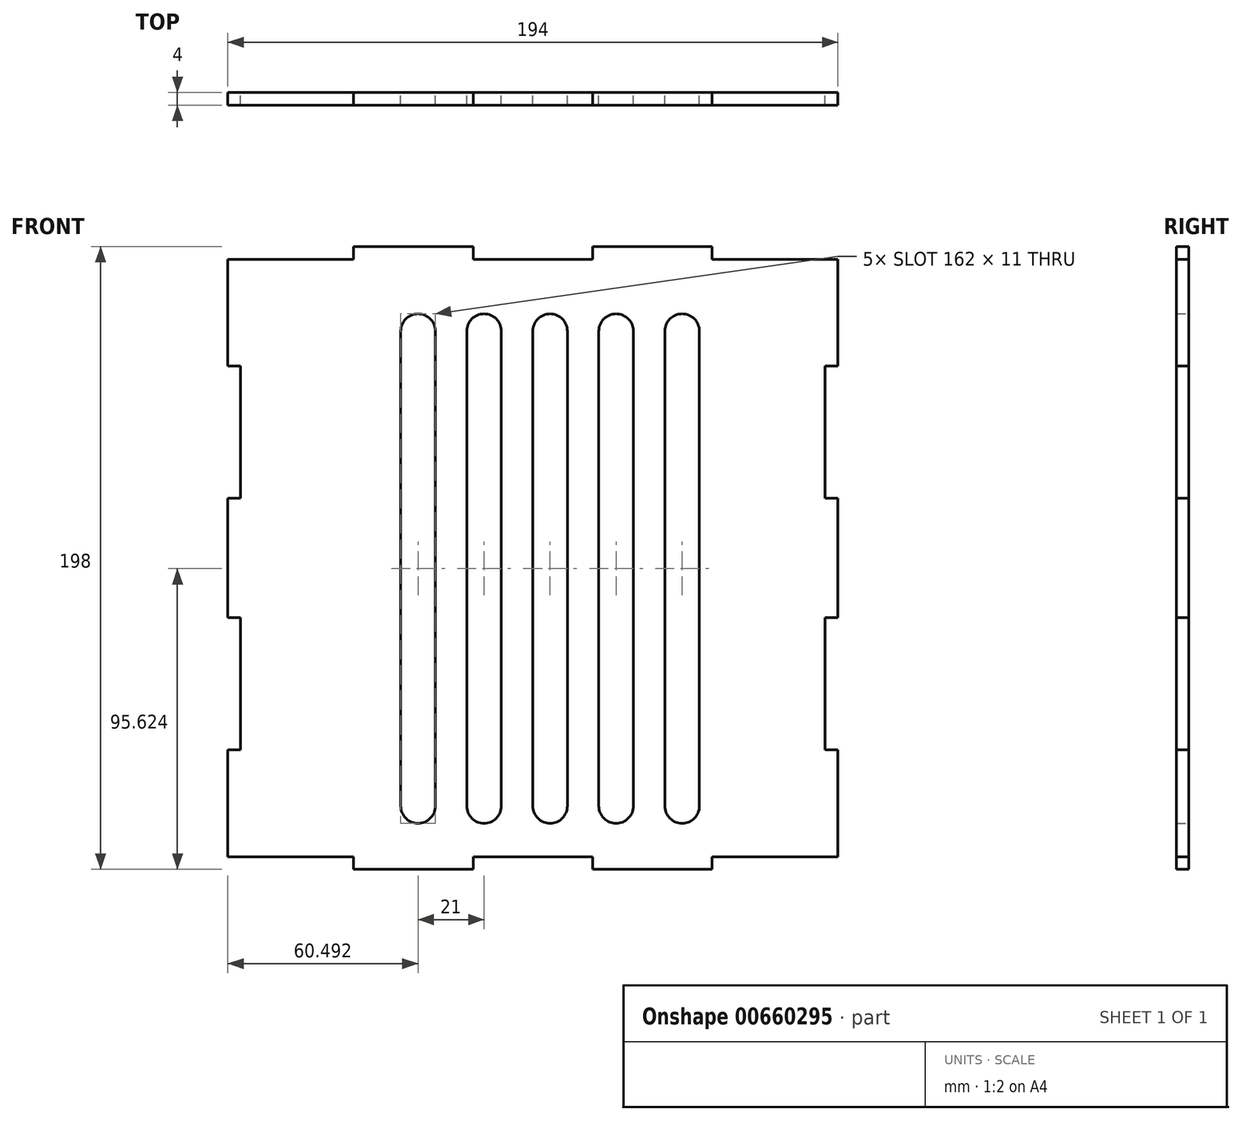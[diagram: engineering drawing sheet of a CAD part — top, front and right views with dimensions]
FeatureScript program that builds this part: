
annotation { "Feature Type Name" : "Feature", "Feature Type Description" : "" }
export const myFeature = defineFeature(function(context is Context, id is Id, definition is map)
    precondition{}
    {
        {
            var Q0;
            Q0=qCreatedBy(makeId("Front.planeOp"),FACE);
            var sketch = newSketch(context, id + "F0", { "sketchPlane" : qUnion([Q0])});
            skLineSegment(sketch, "E0.bottom", {"start": v(0, 0) * mm, "end": v(194, 0) * mm});
            skLineSegment(sketch, "E0.top", {"start": v(0, 198) * mm, "end": v(194, 198) * mm});
            skLineSegment(sketch, "E0.left", {"start": v(0, 0) * mm, "end": v(0, 198) * mm});
            skLineSegment(sketch, "E0.right", {"start": v(194, 0) * mm, "end": v(194, 198) * mm});
            skLineSegment(sketch, "E1.bottom", {"start": v(0, 0) * mm, "end": v(40, 0) * mm});
            skLineSegment(sketch, "E1.top", {"start": v(0, 4) * mm, "end": v(40, 4) * mm});
            skLineSegment(sketch, "E1.left", {"start": v(0, 0) * mm, "end": v(0, 4) * mm});
            skLineSegment(sketch, "E1.right", {"start": v(40, 0) * mm, "end": v(40, 4) * mm});
            skLineSegment(sketch, "E2.bottom", {"start": v(194, 0) * mm, "end": v(154, 0) * mm});
            skLineSegment(sketch, "E2.top", {"start": v(194, 4) * mm, "end": v(154, 4) * mm});
            skLineSegment(sketch, "E2.left", {"start": v(194, 0) * mm, "end": v(194, 4) * mm});
            skLineSegment(sketch, "E2.right", {"start": v(154, 0) * mm, "end": v(154, 4) * mm});
            skLineSegment(sketch, "E3.bottom", {"start": v(78, 0) * mm, "end": v(116, 0) * mm});
            skLineSegment(sketch, "E3.top", {"start": v(78, 4) * mm, "end": v(116, 4) * mm});
            skLineSegment(sketch, "E3.left", {"start": v(78, 0) * mm, "end": v(78, 4) * mm});
            skLineSegment(sketch, "E3.right", {"start": v(116, 0) * mm, "end": v(116, 4) * mm});
            skLineSegment(sketch, "E4.bottom", {"start": v(0, 198) * mm, "end": v(40, 198) * mm});
            skLineSegment(sketch, "E4.top", {"start": v(0, 194) * mm, "end": v(40, 194) * mm});
            skLineSegment(sketch, "E4.left", {"start": v(0, 198) * mm, "end": v(0, 194) * mm});
            skLineSegment(sketch, "E4.right", {"start": v(40, 198) * mm, "end": v(40, 194) * mm});
            skLineSegment(sketch, "E5.bottom", {"start": v(78, 198) * mm, "end": v(116, 198) * mm});
            skLineSegment(sketch, "E5.top", {"start": v(78, 194) * mm, "end": v(116, 194) * mm});
            skLineSegment(sketch, "E5.left", {"start": v(78, 198) * mm, "end": v(78, 194) * mm});
            skLineSegment(sketch, "E5.right", {"start": v(116, 198) * mm, "end": v(116, 194) * mm});
            skLineSegment(sketch, "E6.bottom", {"start": v(194, 198) * mm, "end": v(154, 198) * mm});
            skLineSegment(sketch, "E6.top", {"start": v(194, 194) * mm, "end": v(154, 194) * mm});
            skLineSegment(sketch, "E6.left", {"start": v(194, 198) * mm, "end": v(194, 194) * mm});
            skLineSegment(sketch, "E6.right", {"start": v(154, 198) * mm, "end": v(154, 194) * mm});
            skLineSegment(sketch, "E7.bottom", {"start": v(0, 38) * mm, "end": v(4, 38) * mm});
            skLineSegment(sketch, "E7.top", {"start": v(0, 80) * mm, "end": v(4, 80) * mm});
            skLineSegment(sketch, "E7.left", {"start": v(0, 38) * mm, "end": v(0, 80) * mm});
            skLineSegment(sketch, "E7.right", {"start": v(4, 38) * mm, "end": v(4, 80) * mm});
            skLineSegment(sketch, "E8.bottom", {"start": v(0, 160) * mm, "end": v(4, 160) * mm});
            skLineSegment(sketch, "E8.top", {"start": v(0, 118) * mm, "end": v(4, 118) * mm});
            skLineSegment(sketch, "E8.left", {"start": v(0, 160) * mm, "end": v(0, 118) * mm});
            skLineSegment(sketch, "E8.right", {"start": v(4, 160) * mm, "end": v(4, 118) * mm});
            skLineSegment(sketch, "E9.bottom", {"start": v(194, 80) * mm, "end": v(190, 80) * mm});
            skLineSegment(sketch, "E9.top", {"start": v(194, 38) * mm, "end": v(190, 38) * mm});
            skLineSegment(sketch, "E9.left", {"start": v(194, 80) * mm, "end": v(194, 38) * mm});
            skLineSegment(sketch, "E9.right", {"start": v(190, 80) * mm, "end": v(190, 38) * mm});
            skLineSegment(sketch, "E10.bottom", {"start": v(194, 160) * mm, "end": v(190, 160) * mm});
            skLineSegment(sketch, "E10.top", {"start": v(194, 118) * mm, "end": v(190, 118) * mm});
            skLineSegment(sketch, "E10.left", {"start": v(194, 160) * mm, "end": v(194, 118) * mm});
            skLineSegment(sketch, "E10.right", {"start": v(190, 160) * mm, "end": v(190, 118) * mm});
            skSolve(sketch);
        }
        {
            var Q0;
            {var subQ4=sQuery(id+"F0.wireOp",EDGE,"E1.top");Q0=makeQuery(id+"F0.imprint","IMPRINT",FACE,{"disambiguationData":[TD([[makeQuery(id+"F0.imprint","IMPRINT",EDGE,{"derivedFrom":subQ4}),1.0]])]});}
            extrude(context, id + "F1", {"entities" : qUnion([Q0]), "depth" : 4 * mm, "offsetDistance" : 25 * mm});
        }
        {
            var Q0;
            Q0=qCreatedBy(makeId("Front.planeOp"),FACE);
            var sketch = newSketch(context, id + "F2", { "sketchPlane" : qUnion([Q0])});
            skLineSegment(sketch, "E11.bottom", {"start": v(55, 171.12) * mm, "end": v(66, 171.12) * mm});
            skLineSegment(sketch, "E11.top", {"start": v(55, 20.12) * mm, "end": v(66, 20.12) * mm});
            skLineSegment(sketch, "E11.left", {"start": v(55, 171.12) * mm, "end": v(55, 20.12) * mm});
            skLineSegment(sketch, "E11.right", {"start": v(66, 171.12) * mm, "end": v(66, 20.12) * mm});
            skLineSegment(sketch, "E12.bottom", {"start": v(76, 171.12) * mm, "end": v(87, 171.12) * mm});
            skLineSegment(sketch, "E12.top", {"start": v(76, 20.12) * mm, "end": v(87, 20.12) * mm});
            skLineSegment(sketch, "E12.left", {"start": v(76, 171.12) * mm, "end": v(76, 20.12) * mm});
            skLineSegment(sketch, "E12.right", {"start": v(87, 171.12) * mm, "end": v(87, 20.12) * mm});
            skLineSegment(sketch, "E13.bottom", {"start": v(97, 171.12) * mm, "end": v(108, 171.12) * mm});
            skLineSegment(sketch, "E13.top", {"start": v(97, 20.12) * mm, "end": v(108, 20.12) * mm});
            skLineSegment(sketch, "E13.left", {"start": v(97, 171.12) * mm, "end": v(97, 20.12) * mm});
            skLineSegment(sketch, "E13.right", {"start": v(108, 171.12) * mm, "end": v(108, 20.12) * mm});
            skLineSegment(sketch, "E14.bottom", {"start": v(118, 171.12) * mm, "end": v(129, 171.12) * mm});
            skLineSegment(sketch, "E14.top", {"start": v(118, 20.12) * mm, "end": v(129, 20.12) * mm});
            skLineSegment(sketch, "E14.left", {"start": v(118, 171.12) * mm, "end": v(118, 20.12) * mm});
            skLineSegment(sketch, "E14.right", {"start": v(129, 171.12) * mm, "end": v(129, 20.12) * mm});
            skLineSegment(sketch, "E15.bottom", {"start": v(139, 171.12) * mm, "end": v(150, 171.12) * mm});
            skLineSegment(sketch, "E15.top", {"start": v(139, 20.12) * mm, "end": v(150, 20.12) * mm});
            skLineSegment(sketch, "E15.left", {"start": v(139, 171.12) * mm, "end": v(139, 20.12) * mm});
            skLineSegment(sketch, "E15.right", {"start": v(150, 171.12) * mm, "end": v(150, 20.12) * mm});
            skArc(sketch, "E16", {"start": v(55, 20.12) * mm, "mid": v(60.5, 14.62) * mm, "end": v(66, 20.12) * mm});
            skArc(sketch, "E17", {"start": v(76, 20.12) * mm, "mid": v(81.5, 14.62) * mm, "end": v(87, 20.12) * mm});
            skArc(sketch, "E18", {"start": v(97, 20.12) * mm, "mid": v(102.5, 14.62) * mm, "end": v(108, 20.12) * mm});
            skArc(sketch, "E19", {"start": v(118, 20.12) * mm, "mid": v(123.5, 14.62) * mm, "end": v(129, 20.12) * mm});
            skArc(sketch, "E20", {"start": v(139, 20.12) * mm, "mid": v(144.5, 14.62) * mm, "end": v(150, 20.12) * mm});
            skArc(sketch, "E21", {"start": v(66, 171.12) * mm, "mid": v(60.5, 176.62) * mm, "end": v(55, 171.12) * mm});
            skArc(sketch, "E22", {"start": v(87, 171.12) * mm, "mid": v(81.5, 176.62) * mm, "end": v(76, 171.12) * mm});
            skArc(sketch, "E23", {"start": v(108, 171.12) * mm, "mid": v(102.5, 176.62) * mm, "end": v(97, 171.12) * mm});
            skArc(sketch, "E24", {"start": v(129, 171.12) * mm, "mid": v(123.5, 176.62) * mm, "end": v(118, 171.12) * mm});
            skArc(sketch, "E25", {"start": v(150, 171.12) * mm, "mid": v(144.5, 176.62) * mm, "end": v(139, 171.12) * mm});
            skSolve(sketch);
        }
        {
            var Q0;
            Q0 = qSketchRegion(id + "F2", true);
            extrude(context, id + "F3", {"entities" : qUnion([Q0]), "operationType" : NewBodyOperationType.REMOVE, "depth" : 4 * mm, "offsetDistance" : 25 * mm});
        }
    });
